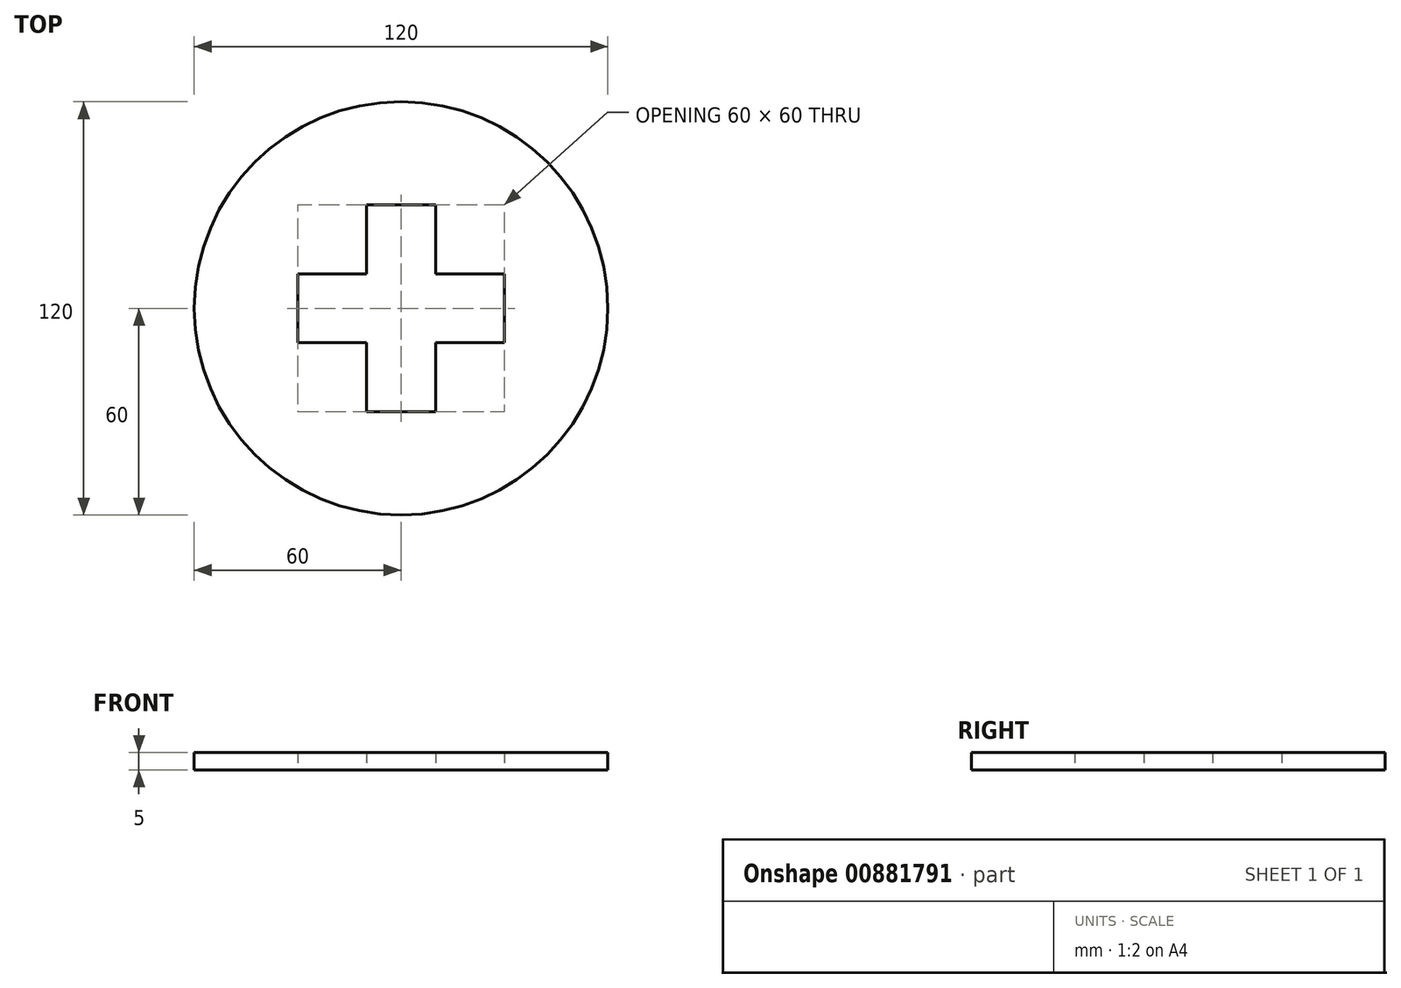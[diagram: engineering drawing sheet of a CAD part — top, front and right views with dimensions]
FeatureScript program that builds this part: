
annotation { "Feature Type Name" : "Feature", "Feature Type Description" : "" }
export const myFeature = defineFeature(function(context is Context, id is Id, definition is map)
    precondition{}
    {
        {
            var Q0;
            Q0=qCreatedBy(makeId("Top.planeOp"),FACE);
            var sketch = newSketch(context, id + "F0", { "sketchPlane" : qUnion([Q0])});
            skCircle(sketch, "E0", {"center": v(0, 0) * mm, "radius": 60 * mm});
            skLineSegment(sketch, "E1", {"start": v(0, 0) * mm, "end": v(-37.32, 0) * mm, "construction": true});
            skLineSegment(sketch, "E2", {"start": v(0, 0) * mm, "end": v(0, 42.9) * mm, "construction": true});
            skLineSegment(sketch, "E3", {"start": v(0, 30) * mm, "end": v(-10, 30) * mm});
            skLineSegment(sketch, "E4", {"start": v(-10, 30) * mm, "end": v(-10, 10) * mm});
            skLineSegment(sketch, "E5", {"start": v(-10, 10) * mm, "end": v(-30, 10) * mm});
            skLineSegment(sketch, "E6", {"start": v(-30, 10) * mm, "end": v(-30, 0) * mm});
            skLineSegment(sketch, "E7.MirrorCS", {"start": v(-30, -10) * mm, "end": v(-30, 0) * mm});
            skLineSegment(sketch, "E8.MirrorCS", {"start": v(-10, -10) * mm, "end": v(-30, -10) * mm});
            skLineSegment(sketch, "E9.MirrorCS", {"start": v(-10, -30) * mm, "end": v(-10, -10) * mm});
            skLineSegment(sketch, "E10.MirrorCS", {"start": v(0, -30) * mm, "end": v(-10, -30) * mm});
            skLineSegment(sketch, "E11.MirrorCS", {"start": v(0, 30) * mm, "end": v(10, 30) * mm});
            skLineSegment(sketch, "E12.MirrorCS", {"start": v(10, 30) * mm, "end": v(10, 10) * mm});
            skLineSegment(sketch, "E13.MirrorCS", {"start": v(10, 10) * mm, "end": v(30, 10) * mm});
            skLineSegment(sketch, "E14.MirrorCS", {"start": v(30, 10) * mm, "end": v(30, 0) * mm});
            skLineSegment(sketch, "E15.MirrorCS", {"start": v(30, -10) * mm, "end": v(30, 0) * mm});
            skLineSegment(sketch, "E16.MirrorCS", {"start": v(10, -10) * mm, "end": v(30, -10) * mm});
            skLineSegment(sketch, "E17.MirrorCS", {"start": v(10, -30) * mm, "end": v(10, -10) * mm});
            skLineSegment(sketch, "E18.MirrorCS", {"start": v(0, -30) * mm, "end": v(10, -30) * mm});
            skSolve(sketch);
        }
        {
            var Q0;
            Q0=qSketchRegion(id+"F0",true);
            extrude(context, id + "F1", {"entities" : qUnion([Q0]), "depth" : 5 * mm, "offsetDistance" : 25 * mm});
        }
    });
